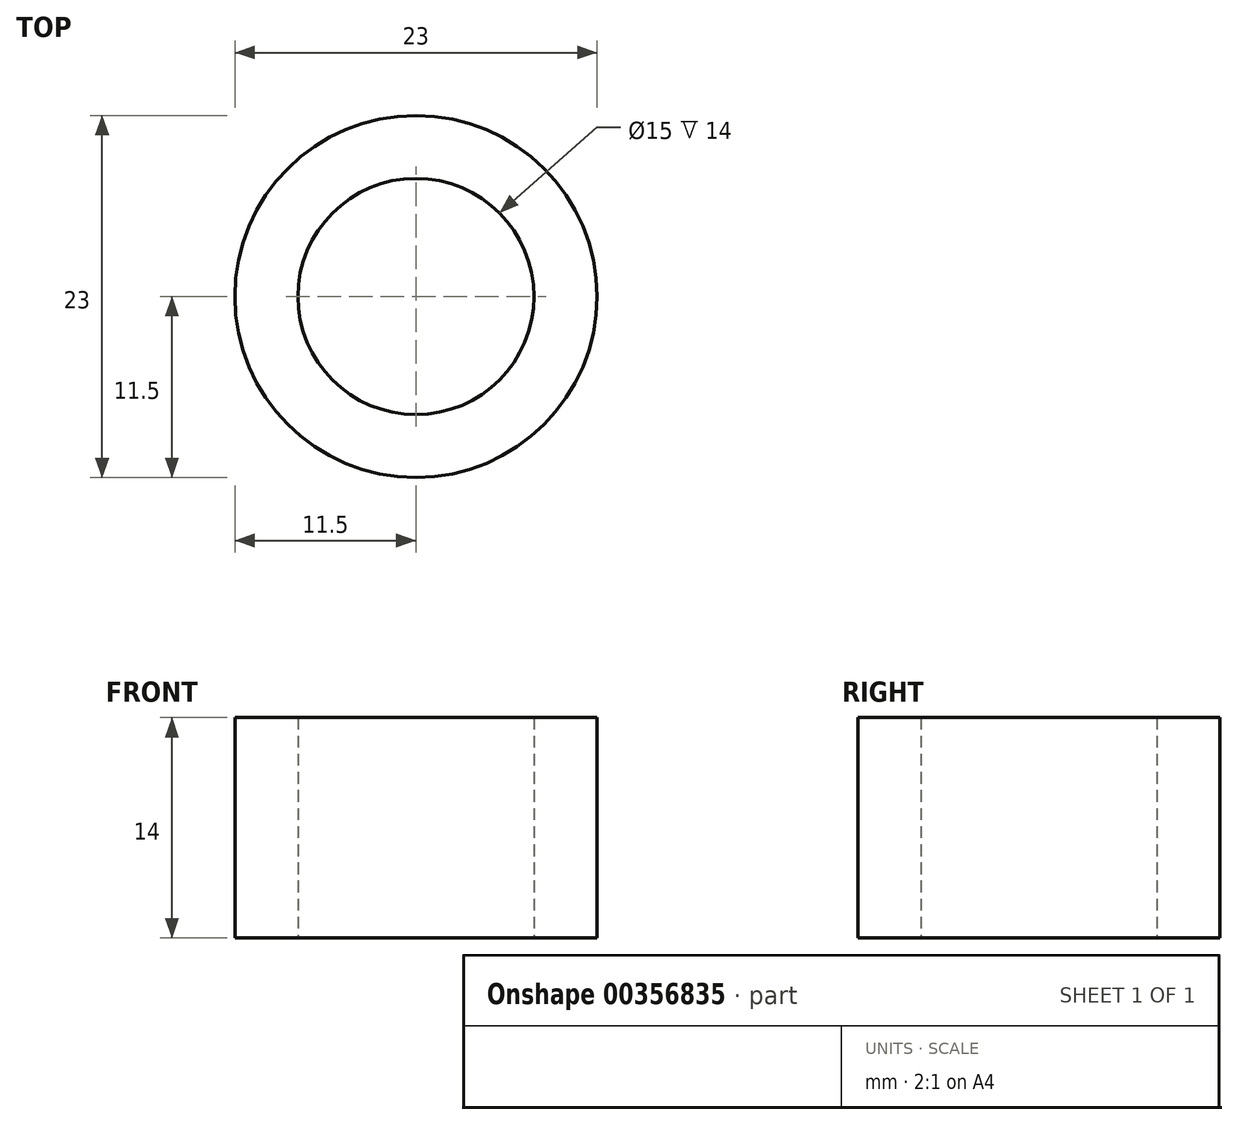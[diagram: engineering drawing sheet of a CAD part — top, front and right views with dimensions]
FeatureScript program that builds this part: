
annotation { "Feature Type Name" : "Feature", "Feature Type Description" : "" }
export const myFeature = defineFeature(function(context is Context, id is Id, definition is map)
    precondition{}
    {
        {
            assignVariable(context, id + "F0", {"name" : "height", "anyValue" : 14});
        }
        {
            var Q0;
            Q0=qCreatedBy(makeId("Top.planeOp"),FACE);
            var sketch = newSketch(context, id + "F1", { "sketchPlane" : qUnion([Q0])});
            skCircle(sketch, "E0", {"center": v(0, 0) * mm, "radius": 7.5 * mm});
            skCircle(sketch, "E1.0", {"center": v(0, 0) * mm, "radius": 11.5 * mm});
            skSolve(sketch);
        }
        {
            var Q0;
            Q0=makeQuery(id+"F1.imprint","IMPRINT",FACE,{"disambiguationData":[TD([[makeQuery(id+"F1.imprint","IMPRINT",EDGE,{"derivedFrom":sQuery(id+"F1.wireOp",EDGE,"E0")}),-1.0]])]});
            extrude(context, id + "F2", {"entities" : qUnion([Q0]), "depth" : (getVariable(context, 'height')) * mm, "offsetDistance" : 25 * mm});
        }
    });
